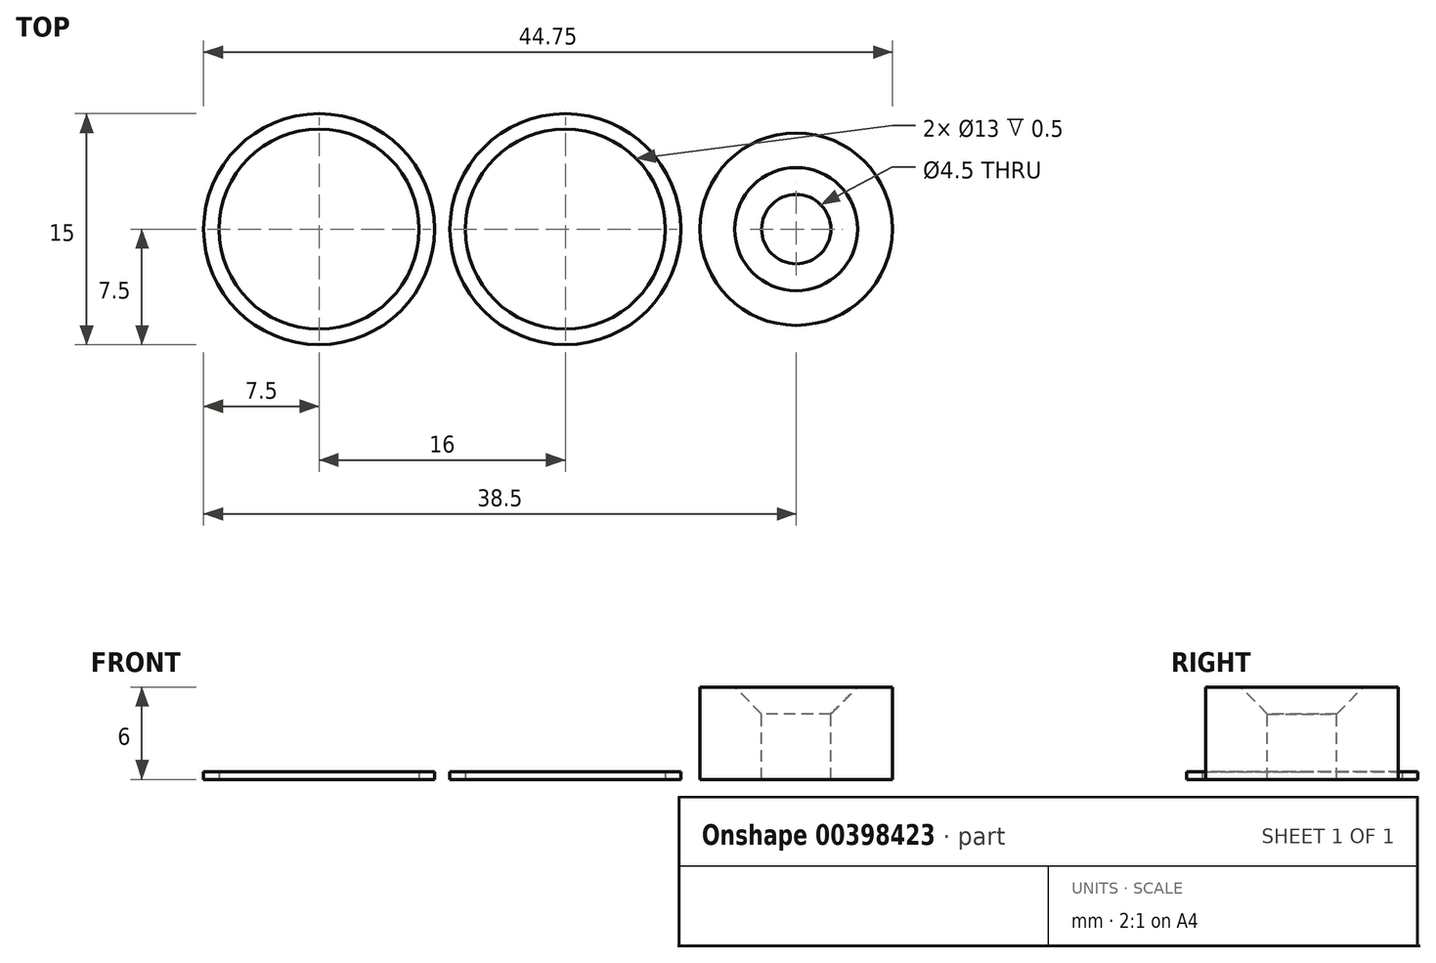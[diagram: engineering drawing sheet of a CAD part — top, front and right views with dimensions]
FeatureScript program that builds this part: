
annotation { "Feature Type Name" : "Feature", "Feature Type Description" : "" }
export const myFeature = defineFeature(function(context is Context, id is Id, definition is map)
    precondition{}
    {
        {
            var Q0;
            Q0=qCreatedBy(makeId("Top.planeOp"),FACE);
            var sketch = newSketch(context, id + "F0", { "sketchPlane" : qUnion([Q0])});
            skCircle(sketch, "E0", {"center": v(0, 0) * mm, "radius": 6.5 * mm});
            skCircle(sketch, "E1", {"center": v(0, 0) * mm, "radius": 7.5 * mm});
            skCircle(sketch, "E2", {"center": v(16, 0) * mm, "radius": 6.5 * mm});
            skCircle(sketch, "E3", {"center": v(16, 0) * mm, "radius": 7.5 * mm});
            skSolve(sketch);
        }
        {
            var Q0;
            Q0=makeQuery(id+"F0.imprint","IMPRINT",FACE,{"disambiguationData":[TD([[makeQuery(id+"F0.imprint","IMPRINT",EDGE,{"derivedFrom":sQuery(id+"F0.wireOp",EDGE,"E0")}),-1.0]])]});
            var Q1;
            Q1=makeQuery(id+"F0.imprint","IMPRINT",FACE,{"disambiguationData":[TD([[makeQuery(id+"F0.imprint","IMPRINT",EDGE,{"derivedFrom":sQuery(id+"F0.wireOp",EDGE,"E2")}),-1.0]])]});
            extrude(context, id + "F1", {"entities" : qUnion([Q0, Q1]), "depth" : 0.5 * mm});
        }
        {
            var Q0;
            Q0=qCreatedBy(makeId("Top.planeOp"),FACE);
            var sketch = newSketch(context, id + "F2", { "sketchPlane" : qUnion([Q0])});
            skCircle(sketch, "E4", {"center": v(31, 0) * mm, "radius": 6.25 * mm});
            skSolve(sketch);
        }
        {
            var Q0;
            Q0=makeQuery(id+"F2.imprint","IMPRINT",FACE,{"disambiguationData":[TD([[makeQuery(id+"F2.imprint","IMPRINT",EDGE,{"derivedFrom":sQuery(id+"F2.wireOp",EDGE,"E4")}),1.0]])]});
            extrude(context, id + "F3", {"entities" : qUnion([Q0]), "depth" : 6 * mm});
        }
        {
            var Q0;
            Q0=makeQuery(id+"F3.opExtrude","CAP_FACE",FACE,{"disambiguationData":[OSD([sQuery(id+"F2.wireOp",EDGE,"E4")])],"isStart":false});
            var sketch = newSketch(context, id + "F4", { "sketchPlane" : qUnion([Q0])});
            skCircle(sketch, "E5", {"center": v(31, 0) * mm, "radius": 4 * mm});
            skSolve(sketch);
        }
        {
            var Q0;
            Q0 = qSketchRegion(id + "F4", true);
            extrude(context, id + "F5", {"entities" : qUnion([Q0]), "operationType" : NewBodyOperationType.REMOVE, "oppositeDirection" : true, "depth" : 2 * mm, "hasDraft" : true, "draftAngle" : 45 * degree, "draftPullDirection" : true});
        }
        {
            var Q0;
            Q0=makeQuery(id+"F3.opExtrude","CAP_FACE",FACE,{"disambiguationData":[OSD([sQuery(id+"F2.wireOp",EDGE,"E4")])],"isStart":false});
            var sketch = newSketch(context, id + "F6", { "sketchPlane" : qUnion([Q0])});
            skCircle(sketch, "E6", {"center": v(31, 0) * mm, "radius": 2.25 * mm});
            skSolve(sketch);
        }
        {
            var Q0;
            Q0 = qSketchRegion(id + "F6", true);
            var Q1;
            Q1=makeQuery(id+"F3.opExtrude","CAP_FACE",FACE,{"disambiguationData":[OSD([sQuery(id+"F2.wireOp",EDGE,"E4")])],"isStart":true});
            extrude(context, id + "F7", {"entities" : qUnion([Q0]), "operationType" : NewBodyOperationType.REMOVE, "endBound" : BoundingType.UP_TO_SURFACE, "oppositeDirection" : true, "endBoundEntityFace" : qUnion([Q1]), "depth" : 25 * mm});
        }
    });
